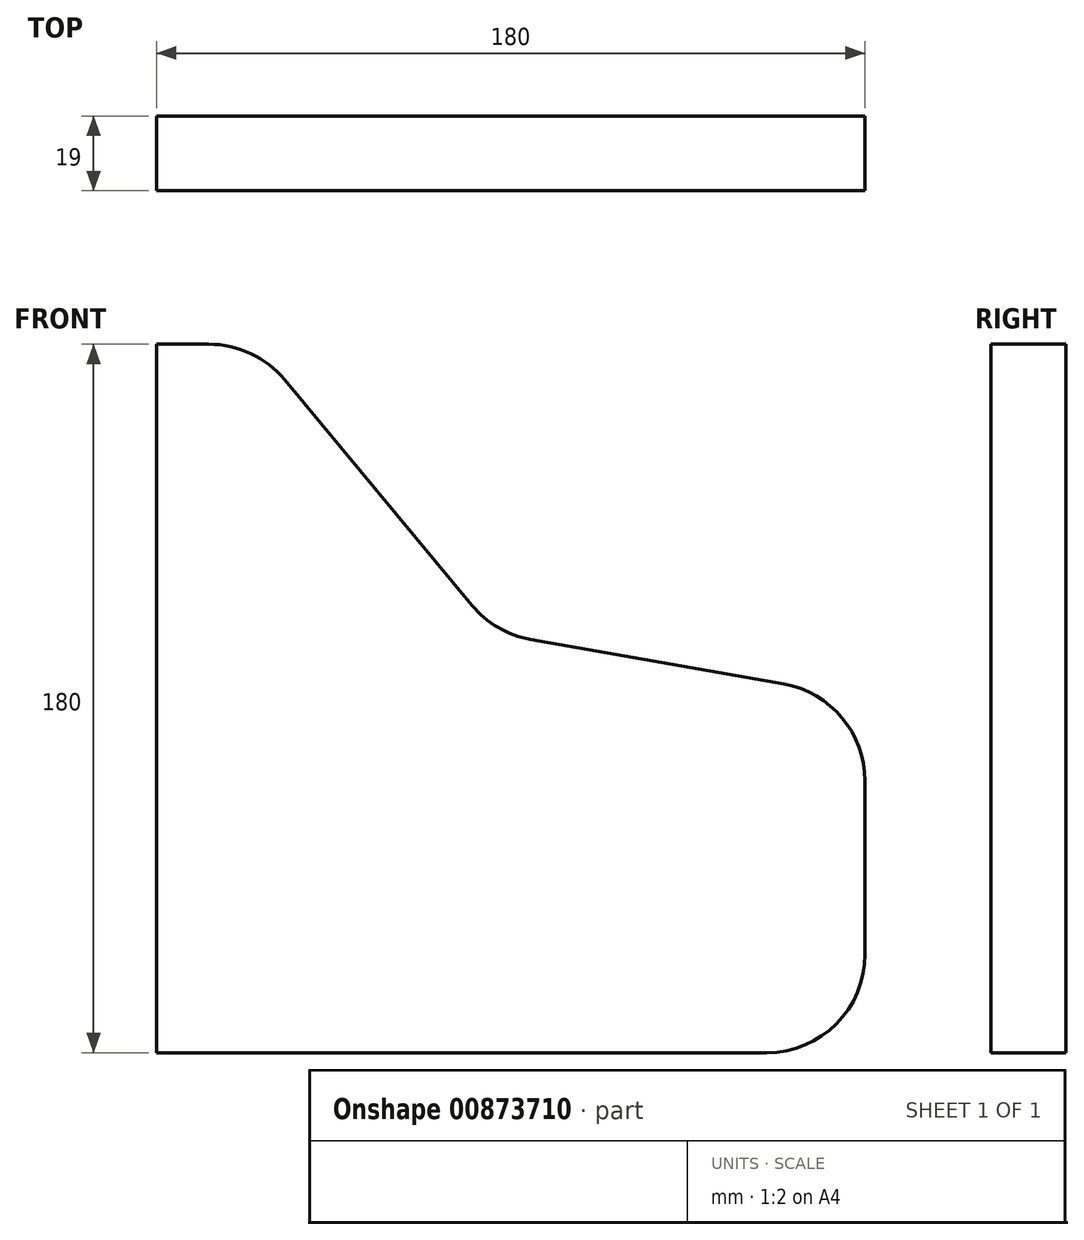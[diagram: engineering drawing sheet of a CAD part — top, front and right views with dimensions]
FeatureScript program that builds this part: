
annotation { "Feature Type Name" : "Feature", "Feature Type Description" : "" }
export const myFeature = defineFeature(function(context is Context, id is Id, definition is map)
    precondition{}
    {
        {
            var Q0;
            Q0=qCreatedBy(makeId("Front.planeOp"),FACE);
            var sketch = newSketch(context, id + "F0", { "sketchPlane" : qUnion([Q0])});
            skLineSegment(sketch, "E0", {"start": v(0, 0) * mm, "end": v(0, -180) * mm});
            skLineSegment(sketch, "E1", {"start": v(0, -180) * mm, "end": v(180, -180) * mm});
            skLineSegment(sketch, "E2", {"start": v(180, -180) * mm, "end": v(180, -90) * mm});
            skLineSegment(sketch, "E3", {"start": v(180, -90) * mm, "end": v(86, -73.42) * mm});
            skLineSegment(sketch, "E4", {"start": v(86, -73.42) * mm, "end": v(25, 0) * mm});
            skLineSegment(sketch, "E5", {"start": v(25, 0) * mm, "end": v(0, 0) * mm});
            skSolve(sketch);
        }
        {
            var Q0;
            Q0=makeQuery(id+"F0.imprint","IMPRINT",FACE,{"disambiguationData":[TD([[makeQuery(id+"F0.imprint","IMPRINT",EDGE,{"derivedFrom":sQuery(id+"F0.wireOp",EDGE,"E0")}),1.0]])]});
            extrude(context, id + "F1", {"entities" : qUnion([Q0]), "depth" : 19 * mm, "offsetDistance" : 25 * mm});
        }
        {
            var Q0;
            Q0=makeQuery(id+"F1.opExtrude","SWEPT_EDGE",EDGE,{"disambiguationData":[OSD([sQuery(id+"F0.wireOp",EDGE,"E4"),sQuery(id+"F0.wireOp",EDGE,"E5")])]});
            var Q1;
            Q1=makeQuery(id+"F1.opExtrude","SWEPT_EDGE",EDGE,{"disambiguationData":[OSD([sQuery(id+"F0.wireOp",EDGE,"E3"),sQuery(id+"F0.wireOp",EDGE,"E4")])]});
            var Q2;
            Q2=makeQuery(id+"F1.opExtrude","SWEPT_EDGE",EDGE,{"disambiguationData":[OSD([sQuery(id+"F0.wireOp",EDGE,"E2"),sQuery(id+"F0.wireOp",EDGE,"E3")])]});
            var Q3;
            Q3=makeQuery(id+"F1.opExtrude","SWEPT_EDGE",EDGE,{"disambiguationData":[OSD([sQuery(id+"F0.wireOp",EDGE,"E1"),sQuery(id+"F0.wireOp",EDGE,"E2")])]});
            fillet(context, id + "F2", {"entities" : qUnion([Q0, Q1, Q2, Q3]), "radius" : 25 * mm, "tangentPropagation" : true, "allowEdgeOverflow" : false});
        }
    });
